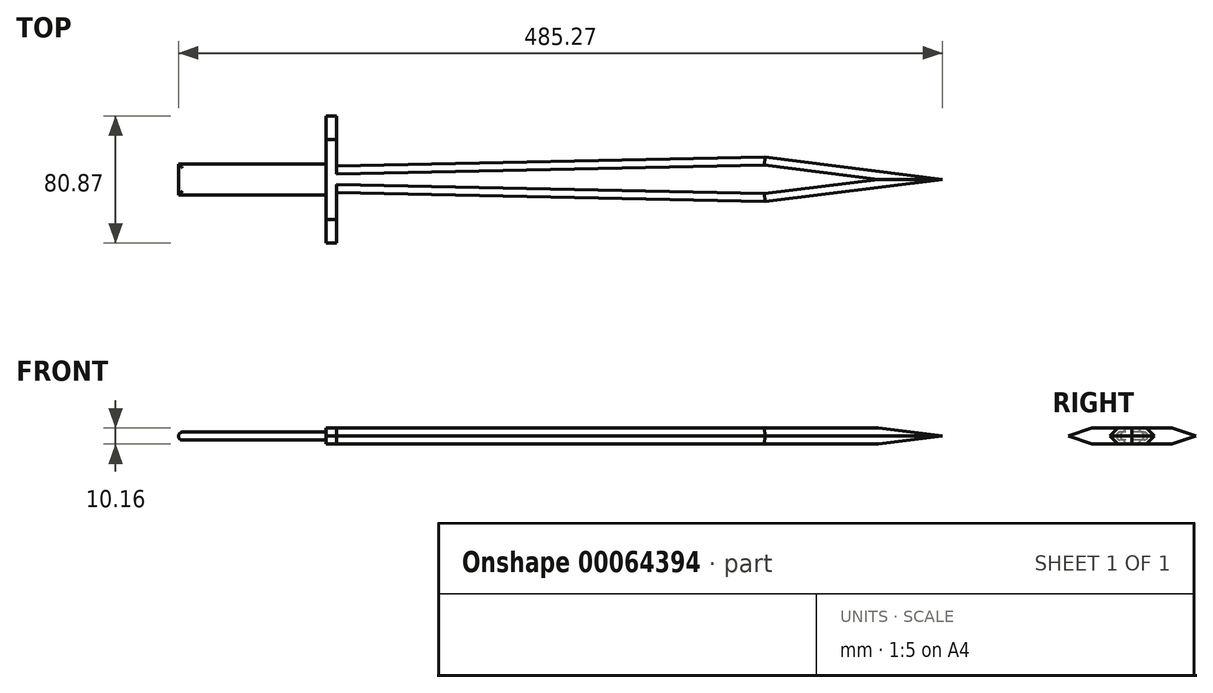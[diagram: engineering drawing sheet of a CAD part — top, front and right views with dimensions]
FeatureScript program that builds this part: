
annotation { "Feature Type Name" : "Feature", "Feature Type Description" : "" }
export const myFeature = defineFeature(function(context is Context, id is Id, definition is map)
    precondition{}
    {
        {
            var Q0;
            Q0=qCreatedBy(makeId("Top.planeOp"),FACE);
            var sketch = newSketch(context, id + "F0", { "sketchPlane" : qUnion([Q0])});
            skLineSegment(sketch, "E0", {"start": v(-167.9, 0) * mm, "end": v(217.1, 0) * mm});
            skLineSegment(sketch, "E1", {"start": v(217.1, 0) * mm, "end": v(104.45, -14.14) * mm});
            skLineSegment(sketch, "E2", {"start": v(-167.9, 0) * mm, "end": v(-167.9, -66.9) * mm, "construction": true});
            skLineSegment(sketch, "E3", {"start": v(104.45, -14.14) * mm, "end": v(-167.9, -8.44) * mm});
            skLineSegment(sketch, "E4", {"start": v(-167.9, -8.44) * mm, "end": v(-167.9, 0) * mm});
            skLineSegment(sketch, "E5.MirrorCS", {"start": v(104.45, 14.14) * mm, "end": v(-167.9, 8.44) * mm});
            skLineSegment(sketch, "E6.MirrorCS", {"start": v(217.1, 0) * mm, "end": v(104.45, 14.14) * mm});
            skLineSegment(sketch, "E7.MirrorCS", {"start": v(-167.9, 8.44) * mm, "end": v(-167.9, 0) * mm});
            skSolve(sketch);
        }
        {
            var Q0;
            Q0 = qSketchRegion(id + "F0", true);
            extrude(context, id + "F1", {"entities" : qUnion([Q0]), "depth" : 5.08 * mm});
        }
        {
            var Q0;
            Q0=makeQuery(id+"F1.opExtrude","CAP_EDGE",EDGE,{"disambiguationData":[OSD([sQuery(id+"F0.wireOp",EDGE,"E3")])],"isStart":false});
            var Q1;
            Q1=makeQuery(id+"F1.opExtrude","CAP_EDGE",EDGE,{"disambiguationData":[OSD([sQuery(id+"F0.wireOp",EDGE,"E5.MirrorCS")])],"isStart":false});
            var Q2;
            Q2=makeQuery(id+"F1.opExtrude","CAP_EDGE",EDGE,{"disambiguationData":[OSD([sQuery(id+"F0.wireOp",EDGE,"E6.MirrorCS")])],"isStart":false});
            var Q3;
            Q3=makeQuery(id+"F1.opExtrude","CAP_EDGE",EDGE,{"disambiguationData":[OSD([sQuery(id+"F0.wireOp",EDGE,"E1")])],"isStart":false});
            chamfer(context, id + "F2", {"entities" : qUnion([Q0, Q1, Q2, Q3]), "width" : 5.08 * mm, "tangentPropagation" : true});
        }
        {
            var Q0;
            Q0=makeQuery(id+"F1.opExtrude","SWEPT_BODY",BODY,{"disambiguationData":[OSD([sQuery(id+"F0.wireOp",EDGE,"E1"),sQuery(id+"F0.wireOp",EDGE,"E3"),sQuery(id+"F0.wireOp",EDGE,"E4"),sQuery(id+"F0.wireOp",EDGE,"E5.MirrorCS"),sQuery(id+"F0.wireOp",EDGE,"E6.MirrorCS"),sQuery(id+"F0.wireOp",EDGE,"E7.MirrorCS")])]});
            var Q1;
            Q1=makeQuery(id+"F1.opExtrude","CAP_FACE",FACE,{"disambiguationData":[OSD([sQuery(id+"F0.wireOp",EDGE,"E1"),sQuery(id+"F0.wireOp",EDGE,"E3"),sQuery(id+"F0.wireOp",EDGE,"E4"),sQuery(id+"F0.wireOp",EDGE,"E5.MirrorCS"),sQuery(id+"F0.wireOp",EDGE,"E6.MirrorCS"),sQuery(id+"F0.wireOp",EDGE,"E7.MirrorCS")])],"isStart":true});
            mirror(context, id + "F3", {"operationType" : NewBodyOperationType.ADD, "entities" : qUnion([Q0]), "mirrorPlane" : qUnion([Q1])});
        }
        {
            var Q0;
            {var subQ0=makeQuery(id+"F1.opExtrude","SWEPT_FACE",FACE,{"disambiguationData":[OSD([sQuery(id+"F0.wireOp",EDGE,"E4"),sQuery(id+"F0.wireOp",EDGE,"E7.MirrorCS")])]});Q0=makeQuery(id+"F3.boolean.opBoolean","MERGE",FACE,{"derivedFrom":[subQ0,makeQuery(id+"F3.opPattern","COPY",FACE,{"derivedFrom":subQ0,"instanceName":"1"})]});}
            var sketch = newSketch(context, id + "F4", { "sketchPlane" : qUnion([Q0])});
            skPoint(sketch, "E8.oppositeSnap0", {"position": v(0, -5.08) * mm});
            skLineSegment(sketch, "E8.bottom", {"start": v(25.4, -5.08) * mm, "end": v(-25.4, -5.08) * mm});
            skLineSegment(sketch, "E8.top", {"start": v(25.4, -5.08) * mm, "end": v(-25.4, -5.08) * mm});
            skLineSegment(sketch, "E8.left", {"start": v(25.4, -5.08) * mm, "end": v(25.4, -5.08) * mm});
            skLineSegment(sketch, "E8.right", {"start": v(-25.4, -5.08) * mm, "end": v(-25.4, -5.08) * mm});
            skLineSegment(sketch, "E9.bottom", {"start": v(-25.4, 5.08) * mm, "end": v(25.4, 5.08) * mm});
            skLineSegment(sketch, "E9.top", {"start": v(-25.4, 5.08) * mm, "end": v(25.4, 5.08) * mm});
            skLineSegment(sketch, "E9.left", {"start": v(-25.4, 5.08) * mm, "end": v(-25.4, 5.08) * mm});
            skLineSegment(sketch, "E9.right", {"start": v(25.4, 5.08) * mm, "end": v(25.4, 5.08) * mm});
            skLineSegment(sketch, "E10", {"start": v(-25.4, -5.08) * mm, "end": v(-25.4, 5.08) * mm, "construction": true});
            skLineSegment(sketch, "E11", {"start": v(25.4, -5.08) * mm, "end": v(25.4, 5.08) * mm, "construction": true});
            skLineSegment(sketch, "E12", {"start": v(-25.4, -5.08) * mm, "end": v(-40.43, 0) * mm});
            skLineSegment(sketch, "E13", {"start": v(-40.43, 0) * mm, "end": v(-25.4, 5.08) * mm});
            skLineSegment(sketch, "E14", {"start": v(25.4, -5.08) * mm, "end": v(40.44, 0) * mm});
            skLineSegment(sketch, "E15", {"start": v(40.44, 0) * mm, "end": v(25.4, 5.08) * mm});
            skSolve(sketch);
        }
        {
            var Q0;
            {var subQ1=sQuery(id+"F4.wireOp",EDGE,"E14");Q0=makeQuery(id+"F4.imprint","IMPRINT",FACE,{"disambiguationData":[TD([[makeQuery(id+"F4.imprint","IMPRINT",EDGE,{"derivedFrom":subQ1}),1.0]])]});}
            var Q1;
            {var subQ0=makeQuery(id+"F1.opExtrude","SWEPT_FACE",FACE,{"disambiguationData":[OSD([sQuery(id+"F0.wireOp",EDGE,"E4"),sQuery(id+"F0.wireOp",EDGE,"E7.MirrorCS")])]});var subQ3=makeQuery(id+"F2.opChamfer","BLEND_EDGE",EDGE,{"blendedFrom":[makeQuery(id+"F1.opExtrude","CAP_EDGE",EDGE,{"disambiguationData":[OSD([sQuery(id+"F0.wireOp",EDGE,"E3")])],"isStart":false}),subQ0],"blendedInto":[subQ0]});Q1=makeQuery(id+"F4.imprint","IMPRINT",FACE,{"disambiguationData":[TD([[makeQuery(id+"F4.imprint","IMPRINT",EDGE,{"derivedFrom":subQ3}),1.0]])]});}
            var Q2;
            {var subQ1=sQuery(id+"F4.wireOp",EDGE,"E12");Q2=makeQuery(id+"F4.imprint","IMPRINT",FACE,{"disambiguationData":[TD([[makeQuery(id+"F4.imprint","IMPRINT",EDGE,{"derivedFrom":subQ1}),-1.0]])]});}
            extrude(context, id + "F5", {"entities" : qUnion([Q0, Q1, Q2]), "operationType" : NewBodyOperationType.ADD, "depth" : 6.35 * mm});
        }
        {
            var Q0;
            Q0=makeQuery(id+"F5.opExtrude","CAP_FACE",FACE,{"disambiguationData":[OSD([sQuery(id+"F4.wireOp",EDGE,"E8.top"),sQuery(id+"F4.wireOp",EDGE,"E9.top"),sQuery(id+"F4.wireOp",EDGE,"E12"),sQuery(id+"F4.wireOp",EDGE,"E13"),sQuery(id+"F4.wireOp",EDGE,"E14"),sQuery(id+"F4.wireOp",EDGE,"E15")])],"isStart":false});
            var sketch = newSketch(context, id + "F6", { "sketchPlane" : qUnion([Q0])});
            skPoint(sketch, "E16.firstSnap0", {"position": v(32.92, 2.54) * mm});
            skLineSegment(sketch, "E16.bottom", {"start": v(-9.95, 2.54) * mm, "end": v(9.96, 2.54) * mm});
            skLineSegment(sketch, "E16.top", {"start": v(-9.95, -2.54) * mm, "end": v(9.96, -2.54) * mm});
            skLineSegment(sketch, "E16.left", {"start": v(-9.95, 2.54) * mm, "end": v(-9.95, -2.54) * mm});
            skLineSegment(sketch, "E16.right", {"start": v(9.96, 2.54) * mm, "end": v(9.96, -2.54) * mm});
            skSolve(sketch);
        }
        {
            var Q0;
            Q0=makeQuery(id+"F6.imprint","IMPRINT",FACE,{"disambiguationData":[TD([[makeQuery(id+"F6.imprint","IMPRINT",EDGE,{"derivedFrom":sQuery(id+"F6.wireOp",EDGE,"E16.bottom")}),-1.0]])]});
            extrude(context, id + "F7", {"entities" : qUnion([Q0]), "operationType" : NewBodyOperationType.ADD, "depth" : 93.92 * mm});
        }
        {
            var Q0;
            Q0=makeQuery(id+"F7.opExtrude","SWEPT_EDGE",EDGE,{"disambiguationData":[OSD([sQuery(id+"F6.wireOp",EDGE,"E16.top"),sQuery(id+"F6.wireOp",EDGE,"E16.left")])]});
            var Q1;
            Q1=makeQuery(id+"F7.opExtrude","SWEPT_EDGE",EDGE,{"disambiguationData":[OSD([sQuery(id+"F6.wireOp",EDGE,"E16.top"),sQuery(id+"F6.wireOp",EDGE,"E16.right")])]});
            var Q2;
            Q2=makeQuery(id+"F7.opExtrude","SWEPT_EDGE",EDGE,{"disambiguationData":[OSD([sQuery(id+"F6.wireOp",EDGE,"E16.bottom"),sQuery(id+"F6.wireOp",EDGE,"E16.left")])]});
            var Q3;
            Q3=makeQuery(id+"F7.opExtrude","SWEPT_EDGE",EDGE,{"disambiguationData":[OSD([sQuery(id+"F6.wireOp",EDGE,"E16.bottom"),sQuery(id+"F6.wireOp",EDGE,"E16.right")])]});
            var Q4;
            Q4=makeQuery(id+"F7.opExtrude","CAP_EDGE",EDGE,{"disambiguationData":[OSD([sQuery(id+"F6.wireOp",EDGE,"E16.bottom")])],"isStart":false});
            var Q5;
            Q5=makeQuery(id+"F7.opExtrude","CAP_EDGE",EDGE,{"disambiguationData":[OSD([sQuery(id+"F6.wireOp",EDGE,"E16.top")])],"isStart":false});
            fillet(context, id + "F8", {"entities" : qUnion([Q0, Q1, Q2, Q3, Q4, Q5]), "radius" : 2.54 * mm, "tangentPropagation" : true, "allowEdgeOverflow" : false});
        }
    });
